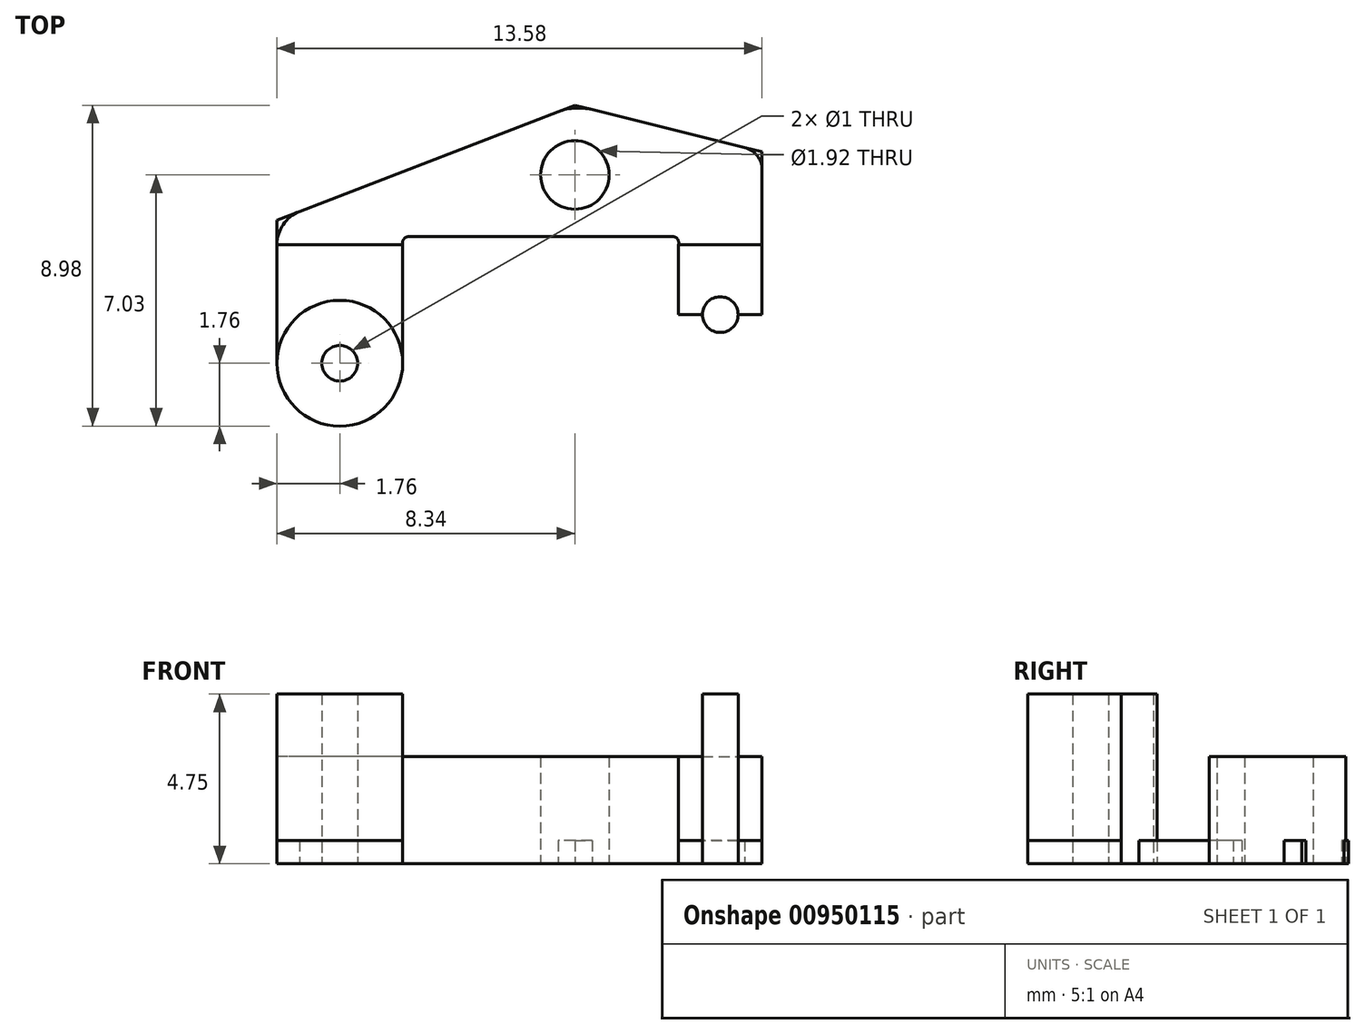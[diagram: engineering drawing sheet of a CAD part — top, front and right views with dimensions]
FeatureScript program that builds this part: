
annotation { "Feature Type Name" : "Feature", "Feature Type Description" : "" }
export const myFeature = defineFeature(function(context is Context, id is Id, definition is map)
    precondition{}
    {
        {
            var Q0;
            Q0=qCreatedBy(makeId("Top.planeOp"),FACE);
            var sketch = newSketch(context, id + "F0", { "sketchPlane" : qUnion([Q0])});
            skLineSegment(sketch, "E0", {"start": v(0, 0) * mm, "end": v(0, 3.9) * mm});
            skLineSegment(sketch, "E1", {"start": v(0, 0) * mm, "end": v(5.24, 0) * mm});
            skLineSegment(sketch, "E2", {"start": v(0, 0) * mm, "end": v(-8.34, 0) * mm});
            skLineSegment(sketch, "E3", {"start": v(0, 3.9) * mm, "end": v(5.24, 2.6) * mm});
            skLineSegment(sketch, "E4", {"start": v(0, 3.9) * mm, "end": v(-8.34, 0.68) * mm});
            skLineSegment(sketch, "E5", {"start": v(5.24, 2.6) * mm, "end": v(5.24, 0) * mm});
            skLineSegment(sketch, "E6", {"start": v(-8.34, 0.68) * mm, "end": v(-8.34, 0) * mm});
            skLineSegment(sketch, "E7", {"start": v(5.24, 0) * mm, "end": v(2.9, 0) * mm});
            skLineSegment(sketch, "E8", {"start": v(4.07, 0) * mm, "end": v(4.07, -1.96) * mm});
            skCircle(sketch, "E9", {"center": v(4.07, -1.96) * mm, "radius": 1.17 * mm});
            skLineSegment(sketch, "E10", {"start": v(5.24, 0) * mm, "end": v(5.24, -1.96) * mm});
            skLineSegment(sketch, "E11", {"start": v(5.24, -1.96) * mm, "end": v(2.9, -1.96) * mm});
            skLineSegment(sketch, "E12", {"start": v(2.9, -1.96) * mm, "end": v(2.9, 0) * mm});
            skLineSegment(sketch, "E13", {"start": v(-8.34, 0) * mm, "end": v(-4.82, 0) * mm});
            skLineSegment(sketch, "E14", {"start": v(-6.58, 0) * mm, "end": v(-6.58, -5.08) * mm});
            skLineSegment(sketch, "E15", {"start": v(-6.58, -5.08) * mm, "end": v(-6.58, -3.32) * mm});
            skCircle(sketch, "E16", {"center": v(-6.58, -3.32) * mm, "radius": 1.76 * mm});
            skLineSegment(sketch, "E17", {"start": v(-4.82, 0) * mm, "end": v(-4.82, -3.32) * mm});
            skLineSegment(sketch, "E18", {"start": v(-8.34, 0) * mm, "end": v(-8.34, -3.32) * mm});
            skLineSegment(sketch, "E19", {"start": v(0, 3.9) * mm, "end": v(0, 1.95) * mm});
            skCircle(sketch, "E20", {"center": v(0, 1.95) * mm, "radius": 0.96 * mm});
            skLineSegment(sketch, "E21", {"start": v(-8.34, 0.68) * mm, "end": v(-7.7, 0.92) * mm});
            skArc(sketch, "E22", {"start": v(-7.7, 0.92) * mm, "mid": v(-8.17, 0.56) * mm, "end": v(-8.34, 0) * mm});
            skLineSegment(sketch, "E23", {"start": v(0, 3.9) * mm, "end": v(-0.47, 3.72) * mm});
            skLineSegment(sketch, "E24", {"start": v(0, 3.9) * mm, "end": v(0.49, 3.78) * mm});
            skArc(sketch, "E25", {"start": v(0.49, 3.78) * mm, "mid": v(0, 3.82) * mm, "end": v(-0.47, 3.72) * mm});
            skLineSegment(sketch, "E26", {"start": v(5.24, 2.6) * mm, "end": v(5.24, 2.1) * mm});
            skLineSegment(sketch, "E27", {"start": v(5.24, 2.6) * mm, "end": v(4.75, 2.72) * mm});
            skArc(sketch, "E28", {"start": v(5.24, 2.1) * mm, "mid": v(5.1, 2.49) * mm, "end": v(4.75, 2.72) * mm});
            skLineSegment(sketch, "E29", {"start": v(-4.65, 0.22) * mm, "end": v(2.74, 0.22) * mm});
            skArc(sketch, "E30", {"start": v(-4.65, 0.22) * mm, "mid": v(-4.8, 0.15) * mm, "end": v(-4.82, 0) * mm});
            skArc(sketch, "E31", {"start": v(2.9, 0) * mm, "mid": v(2.88, 0.15) * mm, "end": v(2.74, 0.22) * mm});
            skCircle(sketch, "E32", {"center": v(4.07, -1.96) * mm, "radius": 0.5 * mm});
            skCircle(sketch, "E33", {"center": v(-6.58, -3.32) * mm, "radius": 0.5 * mm});
            skSolve(sketch);
        }
        {
            var Q0;
            {var subQ4=sQuery(id+"F0.wireOp",EDGE,"E4");Q0=makeQuery(id+"F0.imprint","IMPRINT",FACE,{"disambiguationData":[TD([[makeQuery(id+"F0.imprint","IMPRINT",EDGE,{"derivedFrom":subQ4}),1.0]])]});}
            var Q1;
            {var subQ0=sQuery(id+"F0.wireOp",EDGE,"E17");Q1=makeQuery(id+"F0.imprint","IMPRINT",FACE,{"disambiguationData":[TD([[makeQuery(id+"F0.imprint","IMPRINT",EDGE,{"derivedFrom":subQ0}),-1.0]])]});}
            var Q2;
            {var subQ0=sQuery(id+"F0.wireOp",EDGE,"E18");Q2=makeQuery(id+"F0.imprint","IMPRINT",FACE,{"disambiguationData":[TD([[makeQuery(id+"F0.imprint","IMPRINT",EDGE,{"derivedFrom":subQ0}),1.0]])]});}
            var Q3;
            {var subQ0=sQuery(id+"F0.wireOp",EDGE,"E16");var subQ6=sQuery(id+"F0.wireOp",EDGE,"E14");var subQ7=makeQuery(id+"F0.imprint","INTERSECT",VERTEX,{"derivedFrom":[subQ6,subQ0]});Q3=makeQuery(id+"F0.imprint","IMPRINT",FACE,{"disambiguationData":[TD([[makeQuery(id+"F0.imprint","IMPRINT",EDGE,{"disambiguationData":[TD([[subQ7,-1.0]])],"derivedFrom":subQ6}),-1.0]])]});}
            var Q4;
            {var subQ0=sQuery(id+"F0.wireOp",EDGE,"E16");var subQ2=sQuery(id+"F0.wireOp",EDGE,"E14");var subQ3=makeQuery(id+"F0.imprint","INTERSECT",VERTEX,{"derivedFrom":[subQ2,subQ0]});Q4=makeQuery(id+"F0.imprint","IMPRINT",FACE,{"disambiguationData":[TD([[makeQuery(id+"F0.imprint","IMPRINT",EDGE,{"disambiguationData":[TD([[subQ3,-1.0]])],"derivedFrom":subQ2}),1.0]])]});}
            var Q5;
            {var subQ8=sQuery(id+"F0.wireOp",EDGE,"E3");Q5=makeQuery(id+"F0.imprint","IMPRINT",FACE,{"disambiguationData":[TD([[makeQuery(id+"F0.imprint","IMPRINT",EDGE,{"derivedFrom":subQ8}),-1.0]])]});}
            var Q6;
            {var subQ0=sQuery(id+"F0.wireOp",EDGE,"E12");Q6=makeQuery(id+"F0.imprint","IMPRINT",FACE,{"disambiguationData":[TD([[makeQuery(id+"F0.imprint","IMPRINT",EDGE,{"derivedFrom":subQ0}),-1.0]])]});}
            var Q7;
            {var subQ0=sQuery(id+"F0.wireOp",EDGE,"E10");Q7=makeQuery(id+"F0.imprint","IMPRINT",FACE,{"disambiguationData":[TD([[makeQuery(id+"F0.imprint","IMPRINT",EDGE,{"derivedFrom":subQ0}),-1.0]])]});}
            var Q8;
            {var subQ0=sQuery(id+"F0.wireOp",EDGE,"E9");var subQ1=sQuery(id+"F0.wireOp",EDGE,"E8");var subQ2=makeQuery(id+"F0.imprint","INTERSECT",VERTEX,{"derivedFrom":[subQ1,subQ0]});Q8=makeQuery(id+"F0.imprint","IMPRINT",FACE,{"disambiguationData":[TD([[makeQuery(id+"F0.imprint","IMPRINT",EDGE,{"disambiguationData":[TD([[subQ2,-1.0]])],"derivedFrom":subQ1}),1.0]])]});}
            var Q9;
            {var subQ0=sQuery(id+"F0.wireOp",EDGE,"E9");var subQ1=sQuery(id+"F0.wireOp",EDGE,"E8");var subQ2=makeQuery(id+"F0.imprint","INTERSECT",VERTEX,{"derivedFrom":[subQ1,subQ0]});Q9=makeQuery(id+"F0.imprint","IMPRINT",FACE,{"disambiguationData":[TD([[makeQuery(id+"F0.imprint","IMPRINT",EDGE,{"disambiguationData":[TD([[subQ2,-1.0]])],"derivedFrom":subQ1}),-1.0]])]});}
            var Q10;
            {var subQ0=sQuery(id+"F0.wireOp",EDGE,"E11");var subQ4=sQuery(id+"F0.wireOp",EDGE,"E32");var subQ6=makeQuery(id+"F0.imprint","INTERSECT",VERTEX,{"disambiguationData":[OD(0.0)],"derivedFrom":[subQ0,subQ4]});Q10=makeQuery(id+"F0.imprint","IMPRINT",FACE,{"disambiguationData":[TD([[makeQuery(id+"F0.imprint","IMPRINT",EDGE,{"disambiguationData":[TD([[subQ6,1.0]])],"derivedFrom":subQ4}),-1.0]])]});}
            extrude(context, id + "F1", {"entities" : qUnion([Q0, Q1, Q2, Q3, Q4, Q5, Q6, Q7, Q8, Q9, Q10]), "depth" : .65 * mm, "offsetDistance" : 25 * mm});
        }
        {
            var Q0;
            {var subQ0=sQuery(id+"F0.wireOp",EDGE,"E19");var subQ1=sQuery(id+"F0.wireOp",EDGE,"E0");var subQ2=makeQuery(id+"F0.imprint","INTERSECT",VERTEX,{"derivedFrom":[subQ1,subQ0]});Q0=makeQuery(id+"F0.imprint","IMPRINT",FACE,{"disambiguationData":[TD([[makeQuery(id+"F0.imprint","IMPRINT",EDGE,{"disambiguationData":[TD([[subQ2,1.0]])],"derivedFrom":subQ1}),1.0]])]});}
            var Q1;
            {var subQ0=sQuery(id+"F0.wireOp",EDGE,"E19");var subQ1=sQuery(id+"F0.wireOp",EDGE,"E0");var subQ2=makeQuery(id+"F0.imprint","INTERSECT",VERTEX,{"derivedFrom":[subQ1,subQ0]});Q1=makeQuery(id+"F0.imprint","IMPRINT",FACE,{"disambiguationData":[TD([[makeQuery(id+"F0.imprint","IMPRINT",EDGE,{"disambiguationData":[TD([[subQ2,1.0]])],"derivedFrom":subQ1}),-1.0]])]});}
            extrude(context, id + "F2", {"entities" : qUnion([Q0, Q1]), "depth" : 3 * mm, "offsetDistance" : 25 * mm});
        }
        {
            var Q0;
            {var subQ0=sQuery(id+"F0.wireOp",EDGE,"E15");var subQ1=sQuery(id+"F0.wireOp",EDGE,"E14");var subQ2=makeQuery(id+"F0.imprint","INTERSECT",VERTEX,{"derivedFrom":[subQ1,subQ0]});Q0=makeQuery(id+"F0.imprint","IMPRINT",FACE,{"disambiguationData":[TD([[makeQuery(id+"F0.imprint","IMPRINT",EDGE,{"disambiguationData":[TD([[subQ2,1.0]])],"derivedFrom":subQ1}),1.0]])]});}
            var Q1;
            {var subQ0=sQuery(id+"F0.wireOp",EDGE,"E15");var subQ1=sQuery(id+"F0.wireOp",EDGE,"E14");var subQ2=makeQuery(id+"F0.imprint","INTERSECT",VERTEX,{"derivedFrom":[subQ1,subQ0]});Q1=makeQuery(id+"F0.imprint","IMPRINT",FACE,{"disambiguationData":[TD([[makeQuery(id+"F0.imprint","IMPRINT",EDGE,{"disambiguationData":[TD([[subQ2,1.0]])],"derivedFrom":subQ1}),-1.0]])]});}
            extrude(context, id + "F3", {"entities" : qUnion([Q0, Q1]), "depth" : 4.75 * mm, "offsetDistance" : 25 * mm});
        }
        {
            var Q0;
            {var subQ0=sQuery(id+"F0.wireOp",EDGE,"E11");var subQ1=sQuery(id+"F0.wireOp",EDGE,"E8");var subQ2=makeQuery(id+"F0.imprint","INTERSECT",VERTEX,{"derivedFrom":[subQ1,subQ0]});Q0=makeQuery(id+"F0.imprint","IMPRINT",FACE,{"disambiguationData":[TD([[makeQuery(id+"F0.imprint","IMPRINT",EDGE,{"disambiguationData":[TD([[subQ2,1.0]])],"derivedFrom":subQ1}),1.0]])]});}
            var Q1;
            {var subQ0=sQuery(id+"F0.wireOp",EDGE,"E11");var subQ1=sQuery(id+"F0.wireOp",EDGE,"E8");var subQ2=makeQuery(id+"F0.imprint","INTERSECT",VERTEX,{"derivedFrom":[subQ1,subQ0]});Q1=makeQuery(id+"F0.imprint","IMPRINT",FACE,{"disambiguationData":[TD([[makeQuery(id+"F0.imprint","IMPRINT",EDGE,{"disambiguationData":[TD([[subQ2,1.0]])],"derivedFrom":subQ1}),-1.0]])]});}
            var Q2;
            {var subQ0=sQuery(id+"F0.wireOp",EDGE,"E11");var subQ1=makeQuery(id+"F0.imprint","INTERSECT",VERTEX,{"derivedFrom":[sQuery(id+"F0.wireOp",EDGE,"E8"),subQ0]});Q2=makeQuery(id+"F0.imprint","IMPRINT",FACE,{"disambiguationData":[TD([[makeQuery(id+"F0.imprint","IMPRINT",EDGE,{"disambiguationData":[TD([[subQ1,1.0]])],"derivedFrom":subQ0}),1.0]])]});}
            extrude(context, id + "F4", {"entities" : qUnion([Q0, Q1, Q2]), "depth" : 4.75 * mm, "offsetDistance" : 25 * mm});
        }
    });
